# Revit family: STERN FAUCETS_COOL TFG
name_source: partatom
category: Plumbing Fixtures
units: mm (PartAtom-declared; Revit-internal decimal feet)

## family parameters
Cut with Voids When Loaded = No
Host = Face
Part Type = Normal
Room Calculation Point = Yes
Round Connector Dimension = Use Diameter
Shared = No

## types (2) — shared parameters
BADGE = https://bim.archiproducts.com
DEPTH = 130 mm  [stored 0.426509 ft]
Default Elevation = 1219 mm
Description = Cool TFG - Touch free electronic glass or bottle filler faucet. Activated by IR sensor. For cold or premixed water. Powered by 9V transformer. Filter included. Lead free waterways. Retrofit installation compatibility.
FINISHING MATERIAL = Chrome - Stern
HEIGHT = 241 mm  [stored 0.790682 ft]
INSTALLATION = Lavatory mounted
MATERIAL DESCRIPTION = Finish: Chrome (other finishes avaiable)
MOUNTING OFFSET = 17 mm
Manufacturer = Stern Engineering
Model = Cool TFG
OPERATING PRESSURE = 0.5-8.0 bar / 7.0-116.0 PSI
OPTIONS = Remote control (code 07100005)
PRODUCT SHEET = https://www.archiproducts.com
TECHNICAL SHEET = https://www.sternfaucets.com
URL = http://www.sternfaucets.com
VOLTAGE = 9 V
WATER SUPPLY = Cold or premixed water (1 inlet)
WATER TEMPERATURE = 70°C Maximum
WIDTH = 50 mm  [stored 0.164042 ft]

## per-type parameters (varying)
| type | POWER SUPPLY | PRODUCT CODE |
| COOL TF - 9V TRANSFORMER | 9V Transformer | 280170 (E) |
| COOL TF - 6 X 1,5V BATTERY BOX | Battery Box for 6 X 1.5V AA batteries | 280160 (B) |

note: [stored X ft] marks values corroborated as IEEE doubles in the binary element streams (Revit-internal decimal feet)

## geometry (parser evidence)
native form markers: Blend x2, Sweep x3
no freeform markers — native parametric forms only
